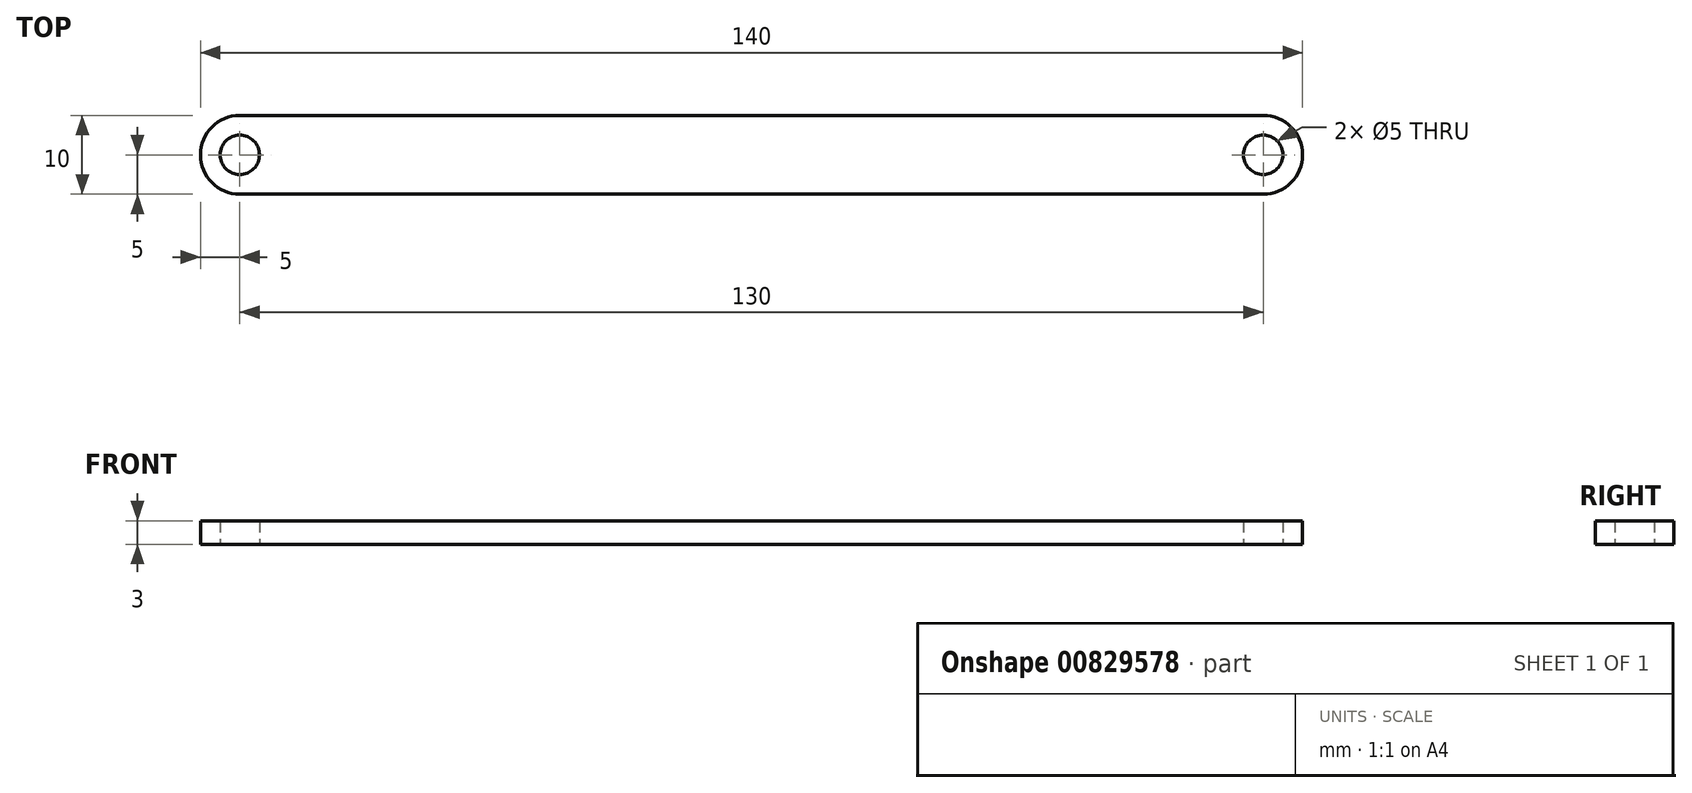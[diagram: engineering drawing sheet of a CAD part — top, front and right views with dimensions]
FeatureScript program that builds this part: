
annotation { "Feature Type Name" : "Feature", "Feature Type Description" : "" }
export const myFeature = defineFeature(function(context is Context, id is Id, definition is map)
    precondition{}
    {
        {
            var Q0;
            Q0=qCreatedBy(makeId("Top.planeOp"),FACE);
            var sketch = newSketch(context, id + "F0", { "sketchPlane" : qUnion([Q0])});
            skArc(sketch, "E0", {"start": v(0, 5) * mm, "mid": v(-5, 0) * mm, "end": v(0, -5) * mm});
            skCircle(sketch, "E1", {"center": v(0, 0) * mm, "radius": 2.5 * mm});
            skCircle(sketch, "E2", {"center": v(130, 0) * mm, "radius": 2.5 * mm});
            skArc(sketch, "E3", {"start": v(130, -5) * mm, "mid": v(135, 0) * mm, "end": v(130, 5) * mm});
            skLineSegment(sketch, "E4", {"start": v(0, 5) * mm, "end": v(130, 5) * mm});
            skLineSegment(sketch, "E5", {"start": v(0, -5) * mm, "end": v(130, -5) * mm});
            skSolve(sketch);
        }
        {
            var Q0;
            Q0=makeQuery(id+"F0.imprint","IMPRINT",FACE,{"disambiguationData":[TD([[makeQuery(id+"F0.imprint","IMPRINT",EDGE,{"derivedFrom":sQuery(id+"F0.wireOp",EDGE,"E0")}),1.0]])]});
            extrude(context, id + "F1", {"entities" : qUnion([Q0]), "depth" : 3 * mm, "offsetDistance" : 25 * mm});
        }
    });
